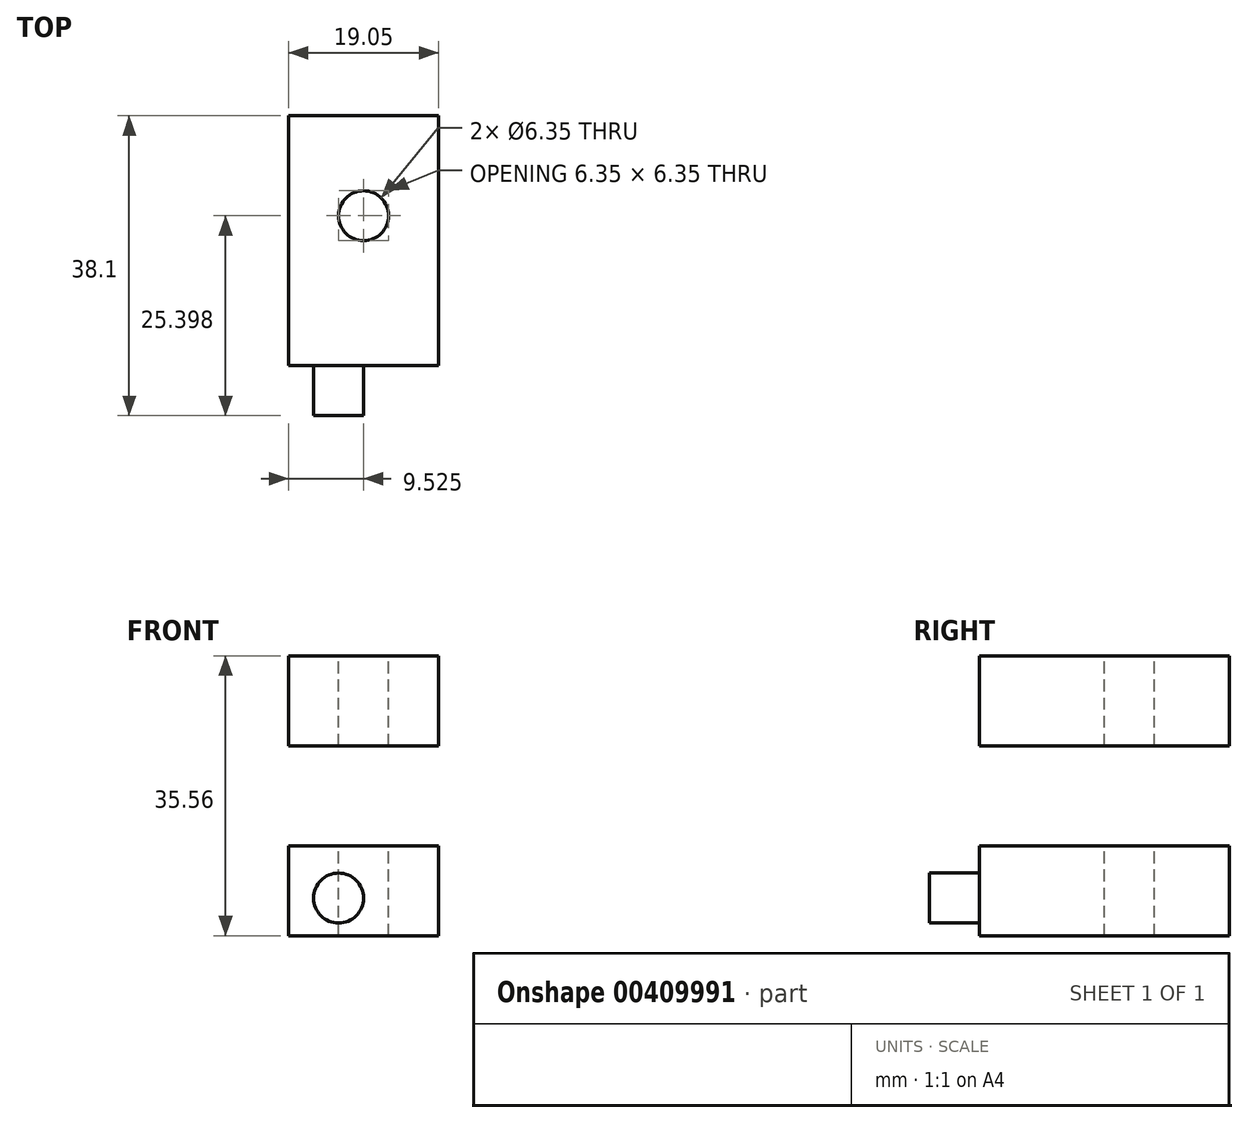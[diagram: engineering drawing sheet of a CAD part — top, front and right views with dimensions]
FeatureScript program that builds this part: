
annotation { "Feature Type Name" : "Feature", "Feature Type Description" : "" }
export const myFeature = defineFeature(function(context is Context, id is Id, definition is map)
    precondition{}
    {
        {
            var Q0;
            Q0=qCreatedBy(makeId("Top.planeOp"),FACE);
            var sketch = newSketch(context, id + "F0", { "sketchPlane" : qUnion([Q0])});
            skLineSegment(sketch, "E0.bottom", {"start": v(0, 0) * mm, "end": v(19.05, 0) * mm});
            skLineSegment(sketch, "E0.top", {"start": v(0, 38.1) * mm, "end": v(19.05, 38.1) * mm});
            skLineSegment(sketch, "E0.left", {"start": v(0, 0) * mm, "end": v(0, 38.1) * mm});
            skLineSegment(sketch, "E0.right", {"start": v(19.05, 0) * mm, "end": v(19.05, 38.1) * mm});
            skSolve(sketch);
        }
        {
            var Q0;
            Q0=makeQuery(id+"F0.imprint","IMPRINT",FACE,{"disambiguationData":[TD([[makeQuery(id+"F0.imprint","IMPRINT",EDGE,{"derivedFrom":sQuery(id+"F0.wireOp",EDGE,"E0.bottom")}),1.0]])]});
            extrude(context, id + "F1", {"entities" : qUnion([Q0]), "oppositeDirection" : true, "depth" : 35.56 * mm});
        }
        {
            var Q0;
            Q0=makeQuery(id+"F1.opExtrude","SWEPT_FACE",FACE,{"disambiguationData":[OSD([sQuery(id+"F0.wireOp",EDGE,"E0.left")])]});
            var sketch = newSketch(context, id + "F2", { "sketchPlane" : qUnion([Q0])});
            skLineSegment(sketch, "E1.bottom", {"start": v(-38.1, -24.13) * mm, "end": v(-6.35, -24.13) * mm});
            skLineSegment(sketch, "E1.top", {"start": v(-38.1, -11.43) * mm, "end": v(-6.35, -11.43) * mm});
            skLineSegment(sketch, "E1.left", {"start": v(-38.1, -24.13) * mm, "end": v(-38.1, -11.43) * mm});
            skLineSegment(sketch, "E1.right", {"start": v(-6.35, -24.13) * mm, "end": v(-6.35, -11.43) * mm});
            skSolve(sketch);
        }
        {
            var Q0;
            Q0=makeQuery(id+"F2.imprint","IMPRINT",FACE,{"disambiguationData":[TD([[makeQuery(id+"F2.imprint","IMPRINT",EDGE,{"derivedFrom":sQuery(id+"F2.wireOp",EDGE,"E1.bottom")}),1.0]])]});
            extrude(context, id + "F3", {"entities" : qUnion([Q0]), "operationType" : NewBodyOperationType.REMOVE, "oppositeDirection" : true, "depth" : 25.4 * mm});
        }
        {
            var Q0;
            Q0=makeQuery(id+"F1.opExtrude","CAP_FACE",FACE,{"disambiguationData":[OSD([sQuery(id+"F0.wireOp",EDGE,"E0.bottom"),sQuery(id+"F0.wireOp",EDGE,"E0.top"),sQuery(id+"F0.wireOp",EDGE,"E0.left"),sQuery(id+"F0.wireOp",EDGE,"E0.right")])],"isStart":true});
            var sketch = newSketch(context, id + "F4", { "sketchPlane" : qUnion([Q0])});
            skLineSegment(sketch, "E2", {"start": v(9.52, 0) * mm, "end": v(9.52, 25.4) * mm});
            skCircle(sketch, "E3", {"center": v(9.52, 25.4) * mm, "radius": 3.18 * mm});
            skSolve(sketch);
        }
        {
            var Q0;
            Q0=makeQuery(id+"F4.imprint","IMPRINT",FACE,{"disambiguationData":[TD([[makeQuery(id+"F4.imprint","IMPRINT",EDGE,{"derivedFrom":sQuery(id+"F4.wireOp",EDGE,"E3")}),1.0]])]});
            extrude(context, id + "F5", {"entities" : qUnion([Q0]), "operationType" : NewBodyOperationType.REMOVE, "endBound" : BoundingType.THROUGH_ALL, "oppositeDirection" : true, "depth" : 25.4 * mm});
        }
        {
            var Q0;
            Q0=makeQuery(id+"F1.opExtrude","SWEPT_FACE",FACE,{"disambiguationData":[OSD([sQuery(id+"F0.wireOp",EDGE,"E0.bottom")])]});
            var sketch = newSketch(context, id + "F6", { "sketchPlane" : qUnion([Q0])});
            skCircle(sketch, "E4", {"center": v(6.35, -4.78) * mm, "radius": 3.18 * mm});
            skLineSegment(sketch, "E5", {"start": v(0, -17.78) * mm, "end": v(6.98, -17.78) * mm});
            skCircle(sketch, "E6.MirrorC", {"center": v(6.35, -30.78) * mm, "radius": 3.18 * mm});
            skSolve(sketch);
        }
        {
            var Q0;
            Q0=makeQuery(id+"F6.imprint","IMPRINT",FACE,{"disambiguationData":[TD([[makeQuery(id+"F6.imprint","IMPRINT",EDGE,{"derivedFrom":sQuery(id+"F6.wireOp",EDGE,"E6.MirrorC")}),-1.0]])]});
            var Q1;
            Q1=makeQuery(id+"F6.imprint","IMPRINT",FACE,{"disambiguationData":[TD([[makeQuery(id+"F6.imprint","IMPRINT",EDGE,{"derivedFrom":sQuery(id+"F6.wireOp",EDGE,"E4")}),1.0]])]});
            extrude(context, id + "F7", {"entities" : qUnion([Q0, Q1]), "operationType" : NewBodyOperationType.REMOVE, "oppositeDirection" : true, "depth" : 6.35 * mm});
        }
    });
